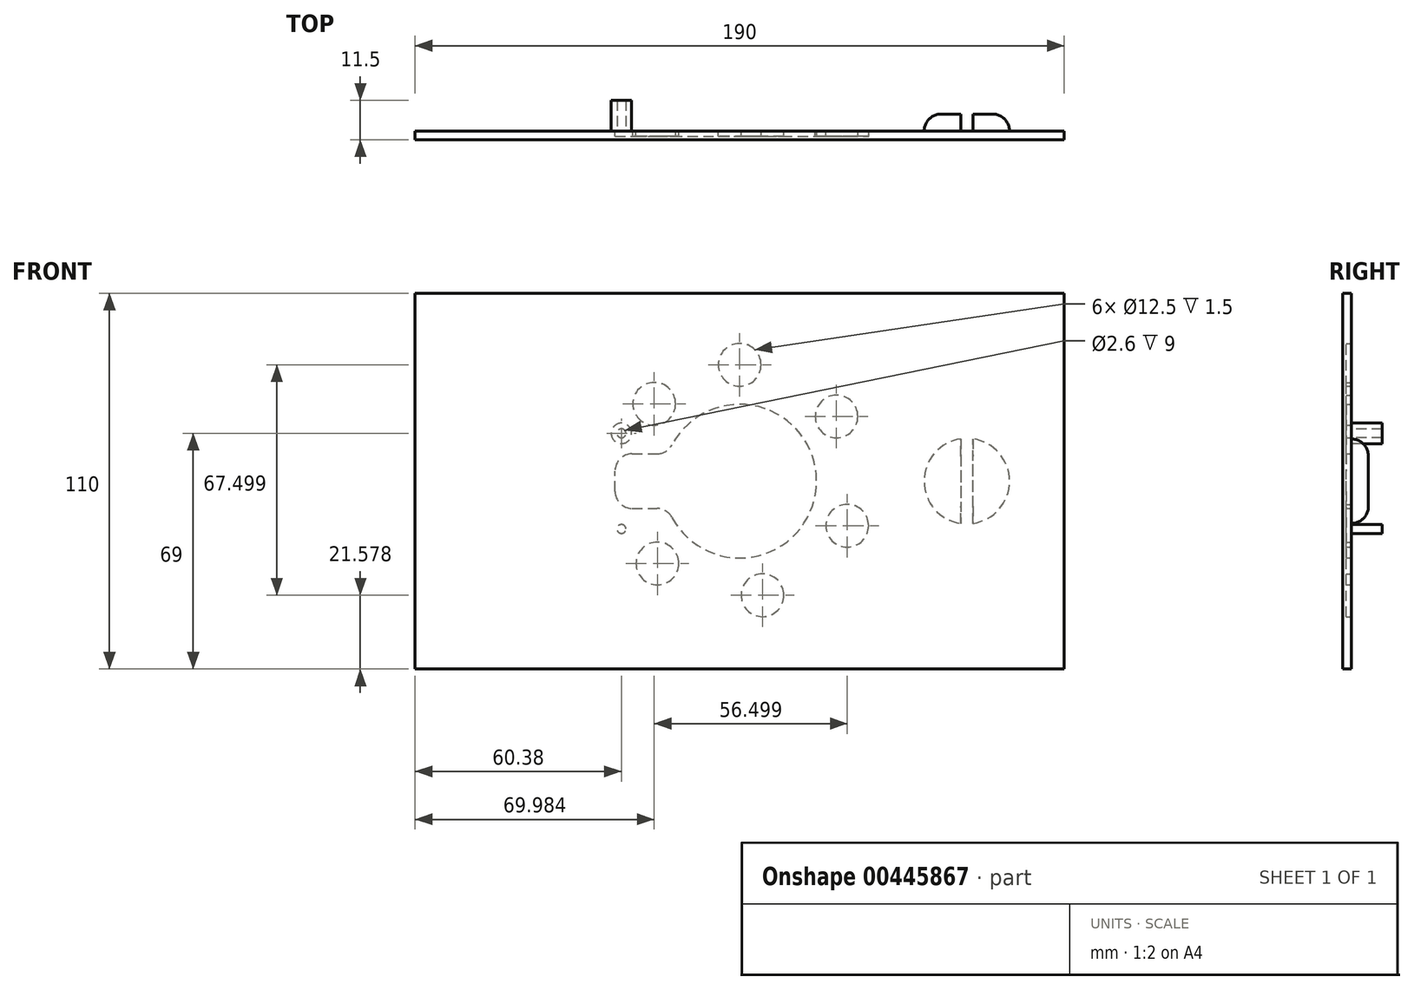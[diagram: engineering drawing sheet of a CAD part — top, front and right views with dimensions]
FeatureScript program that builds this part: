
annotation { "Feature Type Name" : "Feature", "Feature Type Description" : "" }
export const myFeature = defineFeature(function(context is Context, id is Id, definition is map)
    precondition{}
    {
        {
            var Q0;
            Q0=qCreatedBy(makeId("Front.planeOp"),FACE);
            var sketch = newSketch(context, id + "F0", { "sketchPlane" : qUnion([Q0])});
            skLineSegment(sketch, "E0.bottom", {"start": v(95, -55) * mm, "end": v(-95, -55) * mm});
            skLineSegment(sketch, "E0.top", {"start": v(95, 55) * mm, "end": v(-95, 55) * mm});
            skLineSegment(sketch, "E0.left", {"start": v(95, -55) * mm, "end": v(95, 55) * mm});
            skLineSegment(sketch, "E0.right", {"start": v(-95, -55) * mm, "end": v(-95, 55) * mm});
            skLineSegment(sketch, "E1", {"start": v(-95, -50.7) * mm, "end": v(95, -50.7) * mm, "construction": true});
            skCircle(sketch, "E2", {"center": v(-34.62, 14) * mm, "radius": 1.3 * mm});
            skCircle(sketch, "E3.MirrorC", {"center": v(-34.62, -14) * mm, "radius": 1.3 * mm});
            skCircle(sketch, "E4", {"center": v(-34.62, 14) * mm, "radius": 3 * mm});
            skCircle(sketch, "E5", {"center": v(-34.62, -14) * mm, "radius": 3 * mm});
            skArc(sketch, "E6", {"start": v(-19.83, -10.64) * mm, "mid": v(22.5, 0) * mm, "end": v(-19.83, 10.64) * mm});
            skPoint(sketch, "E7.middle", {"position": v(-22.5, 0) * mm});
            skLineSegment(sketch, "E8.bottom", {"start": v(-31.5, -8) * mm, "end": v(-24.23, -8) * mm});
            skLineSegment(sketch, "E8.top", {"start": v(-31.5, 8) * mm, "end": v(-24.23, 8) * mm});
            skLineSegment(sketch, "E8.left", {"start": v(-36.5, -3) * mm, "end": v(-36.5, 3) * mm});
            skPoint(sketch, "E8.right.end.orphan", {"position": v(-8.5, 8) * mm});
            skPoint(sketch, "E8.right.start.orphan", {"position": v(-8.5, -8) * mm});
            skPoint(sketch, "E9.visualSharp", {"position": v(-36.5, 8) * mm});
            skArc(sketch, "E9.filletArc", {"start": v(-31.5, 8) * mm, "mid": v(-35.04, 6.54) * mm, "end": v(-36.5, 3) * mm});
            skPoint(sketch, "E10.visualSharp", {"position": v(-36.5, -8) * mm});
            skArc(sketch, "E10.filletArc", {"start": v(-36.5, -3) * mm, "mid": v(-35.04, -6.54) * mm, "end": v(-31.5, -8) * mm});
            skPoint(sketch, "E11.visualSharp", {"position": v(-21.03, -8) * mm});
            skArc(sketch, "E11.filletArc", {"start": v(-19.83, -10.64) * mm, "mid": v(-21.67, -8.7) * mm, "end": v(-24.23, -8) * mm});
            skPoint(sketch, "E12.visualSharp", {"position": v(-21.03, 8) * mm});
            skArc(sketch, "E12.filletArc", {"start": v(-24.23, 8) * mm, "mid": v(-21.67, 8.7) * mm, "end": v(-19.83, 10.64) * mm});
            skCircle(sketch, "E13", {"center": v(0, 34.08) * mm, "radius": 6.25 * mm});
            skCircle(sketch, "E14", {"center": v(0, 0) * mm, "radius": 27.5 * mm, "construction": true});
            skLineSegment(sketch, "E15.anchor1", {"start": v(0, 0) * mm, "end": v(0, 34.08) * mm, "construction": true});
            skLineSegment(sketch, "E15.anchor2", {"start": v(0, 0) * mm, "end": v(-29.51, 17.04) * mm, "construction": true});
            skCircle(sketch, "E16.1.0", {"center": v(28.33, 18.93) * mm, "radius": 6.25 * mm});
            skCircle(sketch, "E16.2.0", {"center": v(31.48, -13.04) * mm, "radius": 6.25 * mm});
            skCircle(sketch, "E16.3.0", {"center": v(6.65, -33.42) * mm, "radius": 6.25 * mm});
            skCircle(sketch, "E16.4.0", {"center": v(-24.1, -24.1) * mm, "radius": 6.25 * mm});
            skLineSegment(sketch, "E16.anchor2", {"start": v(0, 0) * mm, "end": v(-24.1, -24.1) * mm, "construction": true});
            skCircle(sketch, "E17", {"center": v(-25.02, 22.66) * mm, "radius": 6.25 * mm});
            skLineSegment(sketch, "E18", {"start": v(0, 0) * mm, "end": v(27.5, 0) * mm, "construction": true});
            skCircle(sketch, "E19", {"center": v(66.47, 0) * mm, "radius": 12.5 * mm});
            skLineSegment(sketch, "E20.0", {"start": v(64.72, 0) * mm, "end": v(64.72, 12.38) * mm});
            skLineSegment(sketch, "E20.1", {"start": v(64.72, 0) * mm, "end": v(64.72, -12.5) * mm});
            skLineSegment(sketch, "E21.0", {"start": v(68.22, 0) * mm, "end": v(68.22, 12.5) * mm});
            skLineSegment(sketch, "E22.MirrorCS", {"start": v(68.22, 0) * mm, "end": v(68.22, -12.5) * mm});
            skSolve(sketch);
        }
        {
            var Q0;
            Q0=makeQuery(id+"F0.imprint","IMPRINT",FACE,{"disambiguationData":[TD([[makeQuery(id+"F0.imprint","IMPRINT",EDGE,{"derivedFrom":sQuery(id+"F0.wireOp",EDGE,"E0.bottom")}),-1.0]])]});
            var Q1;
            Q1=makeQuery(id+"F0.imprint","IMPRINT",FACE,{"disambiguationData":[TD([[makeQuery(id+"F0.imprint","IMPRINT",EDGE,{"derivedFrom":sQuery(id+"F0.wireOp",EDGE,"E2")}),1.0]])]});
            var Q2;
            Q2=makeQuery(id+"F0.imprint","IMPRINT",FACE,{"disambiguationData":[TD([[makeQuery(id+"F0.imprint","IMPRINT",EDGE,{"derivedFrom":sQuery(id+"F0.wireOp",EDGE,"E2")}),-1.0]])]});
            var Q3;
            Q3=makeQuery(id+"F0.imprint","IMPRINT",FACE,{"disambiguationData":[TD([[makeQuery(id+"F0.imprint","IMPRINT",EDGE,{"derivedFrom":sQuery(id+"F0.wireOp",EDGE,"E3.MirrorC")}),1.0]])]});
            var Q4;
            Q4=makeQuery(id+"F0.imprint","IMPRINT",FACE,{"disambiguationData":[TD([[makeQuery(id+"F0.imprint","IMPRINT",EDGE,{"derivedFrom":sQuery(id+"F0.wireOp",EDGE,"E3.MirrorC")}),-1.0]])]});
            var Q5;
            Q5=makeQuery(id+"F0.imprint","IMPRINT",FACE,{"disambiguationData":[TD([[makeQuery(id+"F0.imprint","IMPRINT",EDGE,{"derivedFrom":sQuery(id+"F0.wireOp",EDGE,"E6")}),1.0]])]});
            var Q6;
            Q6=makeQuery(id+"F0.imprint","IMPRINT",FACE,{"disambiguationData":[TD([[makeQuery(id+"F0.imprint","IMPRINT",EDGE,{"derivedFrom":sQuery(id+"F0.wireOp",EDGE,"E16.4.0")}),1.0]])]});
            var Q7;
            Q7=makeQuery(id+"F0.imprint","IMPRINT",FACE,{"disambiguationData":[TD([[makeQuery(id+"F0.imprint","IMPRINT",EDGE,{"derivedFrom":sQuery(id+"F0.wireOp",EDGE,"E17")}),1.0]])]});
            var Q8;
            Q8=makeQuery(id+"F0.imprint","IMPRINT",FACE,{"disambiguationData":[TD([[makeQuery(id+"F0.imprint","IMPRINT",EDGE,{"derivedFrom":sQuery(id+"F0.wireOp",EDGE,"E13")}),1.0]])]});
            var Q9;
            Q9=makeQuery(id+"F0.imprint","IMPRINT",FACE,{"disambiguationData":[TD([[makeQuery(id+"F0.imprint","IMPRINT",EDGE,{"derivedFrom":sQuery(id+"F0.wireOp",EDGE,"E16.1.0")}),1.0]])]});
            var Q10;
            Q10=makeQuery(id+"F0.imprint","IMPRINT",FACE,{"disambiguationData":[TD([[makeQuery(id+"F0.imprint","IMPRINT",EDGE,{"derivedFrom":sQuery(id+"F0.wireOp",EDGE,"E16.2.0")}),1.0]])]});
            var Q11;
            Q11=makeQuery(id+"F0.imprint","IMPRINT",FACE,{"disambiguationData":[TD([[makeQuery(id+"F0.imprint","IMPRINT",EDGE,{"derivedFrom":sQuery(id+"F0.wireOp",EDGE,"E16.3.0")}),1.0]])]});
            var Q12;
            Q12=makeQuery(id+"F0.imprint","IMPRINT",FACE,{"disambiguationData":[TD([[makeQuery(id+"F0.imprint","IMPRINT",EDGE,{"derivedFrom":sQuery(id+"F0.wireOp",EDGE,"E19")}),1.0]])]});
            var Q13;
            {var subQ0=sQuery(id+"F0.wireOp",EDGE,"E21.0");var subQ1=sQuery(id+"F0.wireOp",EDGE,"E19");var subQ2=makeQuery(id+"F0.imprint","INTERSECT",VERTEX,{"derivedFrom":[subQ1,subQ0]});Q13=makeQuery(id+"F0.imprint","IMPRINT",FACE,{"disambiguationData":[TD([[makeQuery(id+"F0.imprint","IMPRINT",EDGE,{"disambiguationData":[TD([[subQ2,1.0]])],"derivedFrom":subQ1}),1.0]])]});}
            var Q14;
            {var subQ0=sQuery(id+"F0.wireOp",EDGE,"E20.0");Q14=makeQuery(id+"F0.imprint","IMPRINT",FACE,{"disambiguationData":[TD([[makeQuery(id+"F0.imprint","IMPRINT",EDGE,{"derivedFrom":subQ0}),1.0]])]});}
            extrude(context, id + "F1", {"entities" : qUnion([Q0, Q1, Q2, Q3, Q4, Q5, Q6, Q7, Q8, Q9, Q10, Q11, Q12, Q13, Q14]), "depth" : 2.5 * mm});
        }
        {
            var Q0;
            Q0=makeQuery(id+"F0.imprint","IMPRINT",FACE,{"disambiguationData":[TD([[makeQuery(id+"F0.imprint","IMPRINT",EDGE,{"derivedFrom":sQuery(id+"F0.wireOp",EDGE,"E6")}),1.0]])]});
            var Q1;
            Q1=makeQuery(id+"F0.imprint","IMPRINT",FACE,{"disambiguationData":[TD([[makeQuery(id+"F0.imprint","IMPRINT",EDGE,{"derivedFrom":sQuery(id+"F0.wireOp",EDGE,"E16.4.0")}),1.0]])]});
            var Q2;
            Q2=makeQuery(id+"F0.imprint","IMPRINT",FACE,{"disambiguationData":[TD([[makeQuery(id+"F0.imprint","IMPRINT",EDGE,{"derivedFrom":sQuery(id+"F0.wireOp",EDGE,"E16.3.0")}),1.0]])]});
            var Q3;
            Q3=makeQuery(id+"F0.imprint","IMPRINT",FACE,{"disambiguationData":[TD([[makeQuery(id+"F0.imprint","IMPRINT",EDGE,{"derivedFrom":sQuery(id+"F0.wireOp",EDGE,"E16.2.0")}),1.0]])]});
            var Q4;
            Q4=makeQuery(id+"F0.imprint","IMPRINT",FACE,{"disambiguationData":[TD([[makeQuery(id+"F0.imprint","IMPRINT",EDGE,{"derivedFrom":sQuery(id+"F0.wireOp",EDGE,"E16.1.0")}),1.0]])]});
            var Q5;
            Q5=makeQuery(id+"F0.imprint","IMPRINT",FACE,{"disambiguationData":[TD([[makeQuery(id+"F0.imprint","IMPRINT",EDGE,{"derivedFrom":sQuery(id+"F0.wireOp",EDGE,"E13")}),1.0]])]});
            var Q6;
            Q6=makeQuery(id+"F0.imprint","IMPRINT",FACE,{"disambiguationData":[TD([[makeQuery(id+"F0.imprint","IMPRINT",EDGE,{"derivedFrom":sQuery(id+"F0.wireOp",EDGE,"E17")}),1.0]])]});
            extrude(context, id + "F2", {"entities" : qUnion([Q0, Q1, Q2, Q3, Q4, Q5, Q6]), "operationType" : NewBodyOperationType.REMOVE, "depth" : 1.5 * mm});
        }
        {
            var Q0;
            Q0=makeQuery(id+"F0.imprint","IMPRINT",FACE,{"disambiguationData":[TD([[makeQuery(id+"F0.imprint","IMPRINT",EDGE,{"derivedFrom":sQuery(id+"F0.wireOp",EDGE,"E2")}),-1.0]])]});
            var Q1;
            Q1=makeQuery(id+"F0.imprint","IMPRINT",FACE,{"disambiguationData":[TD([[makeQuery(id+"F0.imprint","IMPRINT",EDGE,{"derivedFrom":sQuery(id+"F0.wireOp",EDGE,"E3.MirrorC")}),1.0]])]});
            extrude(context, id + "F3", {"entities" : qUnion([Q0, Q1]), "operationType" : NewBodyOperationType.ADD, "oppositeDirection" : true, "depth" : 9 * mm});
        }
        {
            var Q0;
            {var subQ0=sQuery(id+"F0.wireOp",EDGE,"E21.0");var subQ1=sQuery(id+"F0.wireOp",EDGE,"E19");var subQ2=makeQuery(id+"F0.imprint","INTERSECT",VERTEX,{"derivedFrom":[subQ1,subQ0]});Q0=makeQuery(id+"F0.imprint","IMPRINT",FACE,{"disambiguationData":[TD([[makeQuery(id+"F0.imprint","IMPRINT",EDGE,{"disambiguationData":[TD([[subQ2,1.0]])],"derivedFrom":subQ1}),1.0]])]});}
            var Q1;
            {var subQ0=sQuery(id+"F0.wireOp",EDGE,"E20.0");Q1=makeQuery(id+"F0.imprint","IMPRINT",FACE,{"disambiguationData":[TD([[makeQuery(id+"F0.imprint","IMPRINT",EDGE,{"derivedFrom":subQ0}),1.0]])]});}
            extrude(context, id + "F4", {"entities" : qUnion([Q0, Q1]), "operationType" : NewBodyOperationType.ADD, "oppositeDirection" : true, "depth" : 5 * mm});
        }
        {
            var Q0;
            Q0=makeQuery(id+"F4.opExtrude","CAP_EDGE",EDGE,{"disambiguationData":[OSD([sQuery(id+"F0.wireOp",EDGE,"E19")])],"isStart":false});
            fillet(context, id + "F5", {"entities" : qUnion([Q0]), "radius" : 5 * mm, "tangentPropagation" : true, "allowEdgeOverflow" : false});
        }
    });
